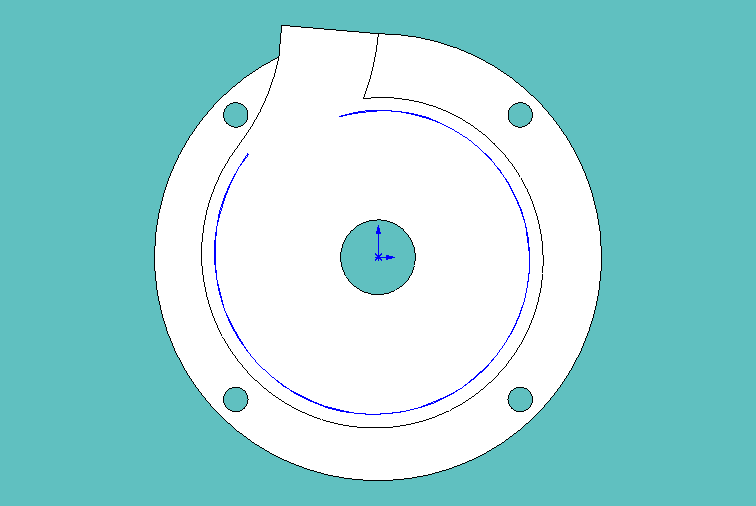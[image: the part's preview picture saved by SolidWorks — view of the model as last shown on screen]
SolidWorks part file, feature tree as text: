
SOLIDWORKS PART (.sldprt)
format: sldprt  version: not decoded by parser v0  size: 559,104 bytes
history: native  units: mm
features: sketch x11, extrude x4, hole x2, material x1, helix x1, cut_extrude x1, plane x1 (+13 scaffold rows collapsed)
feature tree (34):
  scaffold x13  (default folders/planes/origin — collapsed)
  material  "Material <not specified>"
  sketch  "Sketch1"  dims[D1=0.0mm]
  helix  "Helix/Spiral1"  Pitch=5mm
  sketch  "Sketch3"  dims[c1.D3=~36.070819mm c1.D2=18.0mm c2.D3=16.0mm c2.D1=0.0mm c2.D2=15.0mm c3.D1=0.0mm]
  extrude  "Extrude1"  Depth=5mm
  sketch  "Sketch3<3>"  dims[D1=20.0mm D5=3.0mm D6=1.0mm D7=5.0mm]
  cut_extrude  "Cut-Extrude1"  [1 undecoded]
  sketch  "Sketch3<4>"
  sketch  "Sketch5"  dims[D1=3.0mm]
  extrude  "Extrude3"  [1 undecoded]
  sketch  "Sketch6"
  extrude  "Extrude4"  Depth=5mm
  hole  "M16.75 (16.75) Diameter Hole1"  Diameter=16.75mm Depth=5mm
  sketch  "Sketch10"
  sketch  "Sketch9"  dims[hole-wizard template sketch: 59 standard entries collapsed; hole parameters kept: c18.Thru Hole Dia.=16.75mm c18.Thru Hole Depth=5.0mm]
  plane  "Plane4"
  sketch  "Sketch15"  dims[D1=0.0mm]
  extrude  "Extrude5"  [1 undecoded]
  hole  "M13.5 (13.5) Diameter Hole1"  Diameter=13.6mm Depth=10mm
  sketch  "Sketch17"
  sketch  "Sketch16"  dims[hole-wizard template sketch: 46 standard entries collapsed; hole parameters kept: c15.Hole Dia.=13.6mm c15.Hole Depth=10.0mm c15.D3=~14.816244mm c15.Drill Angle=118.0deg]
decode coverage: 12 of 19 modeling features carry decoded parameters
note: ~ marks probable driven/reference dimensions
note: 3 parameter values undecoded
summary: no parameter record found for 3 features
note: suppression state not decoded; provenance and decode notes live in map.json
